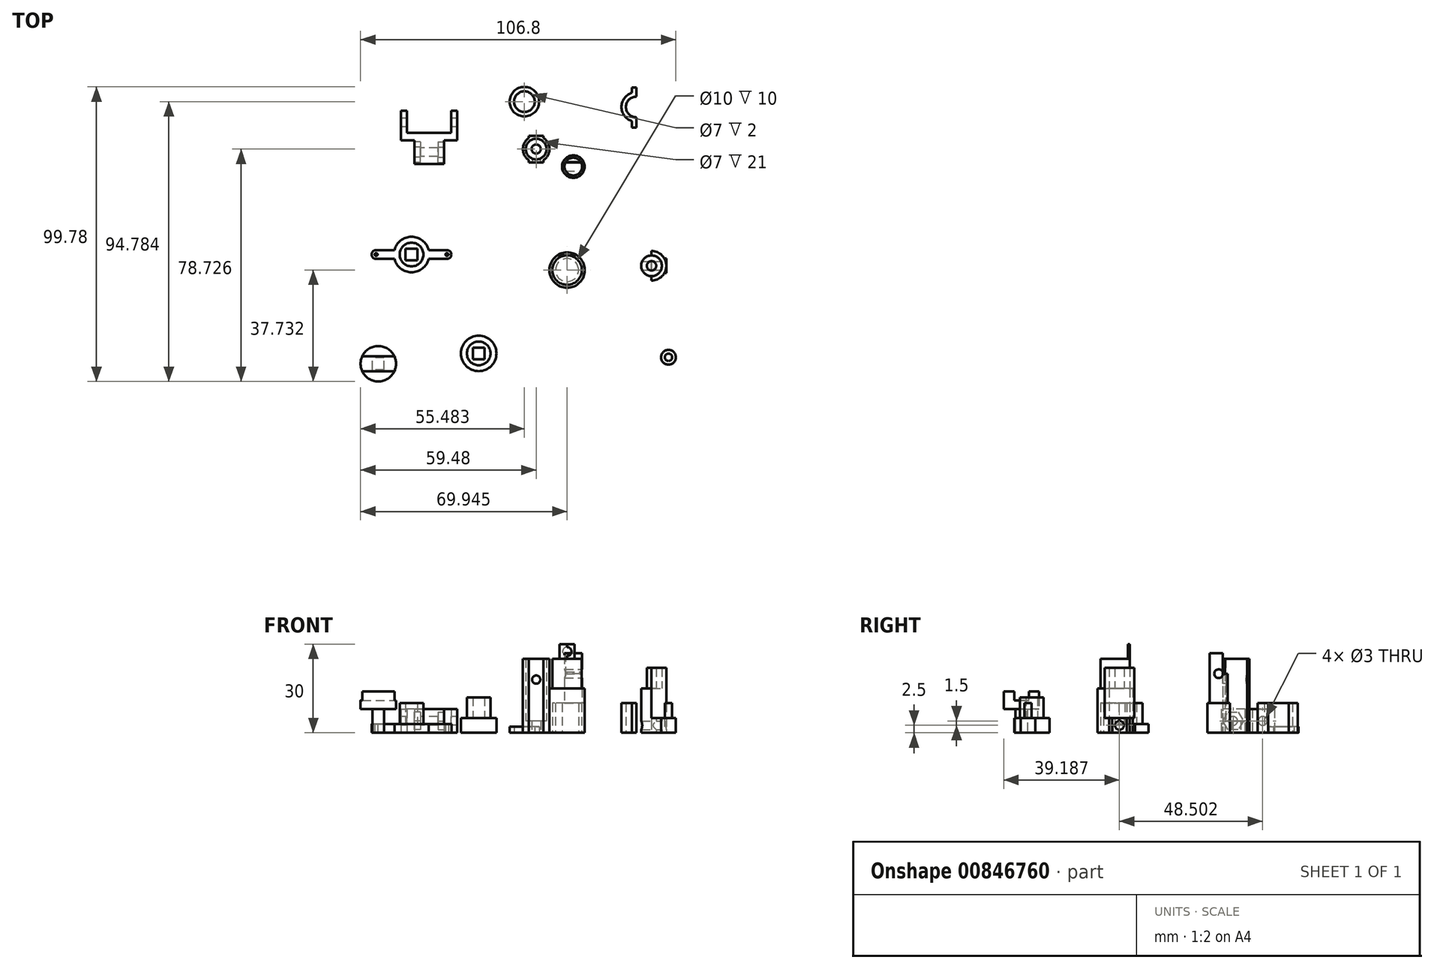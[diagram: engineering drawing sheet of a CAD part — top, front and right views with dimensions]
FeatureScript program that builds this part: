
annotation { "Feature Type Name" : "Feature", "Feature Type Description" : "" }
export const myFeature = defineFeature(function(context is Context, id is Id, definition is map)
    precondition{}
    {
        {
            var Q0;
            Q0=qCreatedBy(makeId("Top.planeOp"),FACE);
            var sketch = newSketch(context, id + "F0", { "sketchPlane" : qUnion([Q0])});
            skLineSegment(sketch, "E0.bottom", {"start": v(-39.48, 20.74) * mm, "end": v(-29.48, 20.74) * mm});
            skLineSegment(sketch, "E0.top", {"start": v(-39.48, 12.74) * mm, "end": v(-29.48, 12.74) * mm});
            skLineSegment(sketch, "E0.left", {"start": v(-39.48, 20.74) * mm, "end": v(-39.48, 12.74) * mm});
            skLineSegment(sketch, "E0.right", {"start": v(-29.48, 20.74) * mm, "end": v(-29.48, 12.74) * mm});
            skLineSegment(sketch, "E1", {"start": v(-39.48, 20.74) * mm, "end": v(-43.98, 20.74) * mm});
            skLineSegment(sketch, "E2", {"start": v(-29.48, 20.74) * mm, "end": v(-24.98, 20.74) * mm});
            skLineSegment(sketch, "E3", {"start": v(-43.98, 20.74) * mm, "end": v(-43.98, 30.74) * mm});
            skLineSegment(sketch, "E4", {"start": v(-24.98, 20.74) * mm, "end": v(-24.98, 30.74) * mm});
            skLineSegment(sketch, "E5", {"start": v(-24.98, 23.24) * mm, "end": v(-43.98, 23.24) * mm});
            skLineSegment(sketch, "E6", {"start": v(-26.98, 30.74) * mm, "end": v(-24.98, 30.74) * mm});
            skLineSegment(sketch, "E7", {"start": v(-43.98, 30.74) * mm, "end": v(-41.98, 30.74) * mm});
            skLineSegment(sketch, "E8", {"start": v(-41.98, 30.74) * mm, "end": v(-41.98, 23.24) * mm});
            skLineSegment(sketch, "E9", {"start": v(-26.98, 30.74) * mm, "end": v(-26.98, 23.24) * mm});
            skSolve(sketch);
        }
        {
            var Q0;
            Q0 = qSketchRegion(id + "F0", true);
            extrude(context, id + "F1", {"entities" : qUnion([Q0]), "depth" : 8 * mm, "offsetDistance" : 25 * mm});
        }
        {
            var Q0;
            Q0=makeQuery(id+"F1.opExtrude","SWEPT_FACE",FACE,{"disambiguationData":[OSD([sQuery(id+"F0.wireOp",EDGE,"E0.left")])]});
            var sketch = newSketch(context, id + "F2", { "sketchPlane" : qUnion([Q0])});
            skCircle(sketch, "E10", {"center": v(-16.74, 4) * mm, "radius": 1.5 * mm});
            skSolve(sketch);
        }
        {
            var Q0;
            Q0=makeQuery(id+"F2.imprint","IMPRINT",FACE,{"disambiguationData":[TD([[makeQuery(id+"F2.imprint","IMPRINT",EDGE,{"derivedFrom":sQuery(id+"F2.wireOp",EDGE,"E10")}),1.0]])]});
            extrude(context, id + "F3", {"entities" : qUnion([Q0]), "operationType" : NewBodyOperationType.REMOVE, "oppositeDirection" : true, "depth" : 25 * mm, "offsetDistance" : 25 * mm});
        }
        {
            var Q0;
            Q0=makeQuery(id+"F1.opExtrude","SWEPT_FACE",FACE,{"disambiguationData":[OSD([sQuery(id+"F0.wireOp",EDGE,"E3")])]});
            var sketch = newSketch(context, id + "F4", { "sketchPlane" : qUnion([Q0])});
            skCircle(sketch, "E11", {"center": v(-26.74, 4) * mm, "radius": 1.5 * mm});
            skSolve(sketch);
        }
        {
            var Q0;
            Q0=makeQuery(id+"F4.imprint","IMPRINT",FACE,{"disambiguationData":[TD([[makeQuery(id+"F4.imprint","IMPRINT",EDGE,{"derivedFrom":sQuery(id+"F4.wireOp",EDGE,"E11")}),1.0]])]});
            extrude(context, id + "F5", {"entities" : qUnion([Q0]), "operationType" : NewBodyOperationType.REMOVE, "oppositeDirection" : true, "depth" : 25 * mm, "offsetDistance" : 25 * mm});
        }
        {
            var Q0;
            Q0=qCreatedBy(makeId("Top.planeOp"),FACE);
            var sketch = newSketch(context, id + "F6", { "sketchPlane" : qUnion([Q0])});
            skCircle(sketch, "E12", {"center": v(40.86, -21.76) * mm, "radius": 5 * mm});
            skCircle(sketch, "E13", {"center": v(40.86, -21.76) * mm, "radius": 3.5 * mm});
            skCircle(sketch, "E14", {"center": v(40.86, -21.76) * mm, "radius": 1.6 * mm});
            skLineSegment(sketch, "E15", {"start": v(40.86, -26.76) * mm, "end": v(40.86, -16.76) * mm});
            skLineSegment(sketch, "E16", {"start": v(45.86, -21.76) * mm, "end": v(45.86, -19.26) * mm});
            skLineSegment(sketch, "E17", {"start": v(45.86, -21.76) * mm, "end": v(45.86, -24.26) * mm});
            skLineSegment(sketch, "E18", {"start": v(45.86, -19.26) * mm, "end": v(45.19, -19.26) * mm});
            skLineSegment(sketch, "E19", {"start": v(45.86, -24.26) * mm, "end": v(45.19, -24.26) * mm});
            skSolve(sketch);
        }
        {
            var Q0;
            Q0=makeQuery(id+"F6.imprint","IMPRINT",FACE,{"disambiguationData":[TD([[makeQuery(id+"F6.imprint","IMPRINT",EDGE,{"derivedFrom":sQuery(id+"F6.wireOp",EDGE,"E13")}),1.0]])]});
            extrude(context, id + "F7", {"entities" : qUnion([Q0]), "depth" : 15 * mm, "offsetDistance" : 25 * mm});
        }
        {
            var Q0;
            Q0=makeQuery(id+"F6.imprint","IMPRINT",FACE,{"disambiguationData":[TD([[makeQuery(id+"F6.imprint","IMPRINT",EDGE,{"derivedFrom":sQuery(id+"F6.wireOp",EDGE,"E12")}),1.0]])]});
            var Q1;
            Q1=makeQuery(id+"F6.imprint","IMPRINT",FACE,{"disambiguationData":[TD([[makeQuery(id+"F6.imprint","IMPRINT",EDGE,{"derivedFrom":sQuery(id+"F6.wireOp",EDGE,"E14")}),1.0]])]});
            var Q2;
            {var subQ0=sQuery(id+"F6.wireOp",EDGE,"E15");var subQ1=sQuery(id+"F6.wireOp",EDGE,"E12");var subQ2=makeQuery(id+"F6.imprint","INTERSECT",VERTEX,{"disambiguationData":[OD(0.0)],"derivedFrom":[subQ1,subQ0]});Q2=makeQuery(id+"F6.imprint","IMPRINT",FACE,{"disambiguationData":[TD([[makeQuery(id+"F6.imprint","IMPRINT",EDGE,{"disambiguationData":[TD([[subQ2,1.0]])],"derivedFrom":subQ1}),1.0]])]});}
            extrude(context, id + "F8", {"entities" : qUnion([Q0, Q1, Q2]), "operationType" : NewBodyOperationType.ADD, "depth" : 22 * mm, "offsetDistance" : 25 * mm});
        }
        {
            var Q0;
            {var subQ0=sQuery(id+"F6.wireOp",EDGE,"E15");var subQ1=sQuery(id+"F6.wireOp",EDGE,"E12");var subQ2=makeQuery(id+"F6.imprint","INTERSECT",VERTEX,{"disambiguationData":[OD(0.0)],"derivedFrom":[subQ1,subQ0]});Q0=makeQuery(id+"F6.imprint","IMPRINT",FACE,{"disambiguationData":[TD([[makeQuery(id+"F6.imprint","IMPRINT",EDGE,{"disambiguationData":[TD([[subQ2,1.0]])],"derivedFrom":subQ1}),1.0]])]});}
            var Q1;
            {var subQ0=sQuery(id+"F6.wireOp",EDGE,"E15");var subQ1=sQuery(id+"F6.wireOp",EDGE,"E14");var subQ2=makeQuery(id+"F6.imprint","INTERSECT",VERTEX,{"disambiguationData":[OD(0.0)],"derivedFrom":[subQ1,subQ0]});Q1=makeQuery(id+"F6.imprint","IMPRINT",FACE,{"disambiguationData":[TD([[makeQuery(id+"F6.imprint","IMPRINT",EDGE,{"disambiguationData":[TD([[subQ2,-1.0]])],"derivedFrom":subQ1}),1.0]])]});}
            extrude(context, id + "F9", {"entities" : qUnion([Q0, Q1]), "operationType" : NewBodyOperationType.REMOVE, "depth" : 5 * mm, "offsetDistance" : 25 * mm});
        }
        {
            var Q0;
            {var subQ0=sQuery(id+"F6.wireOp",EDGE,"E17");Q0=makeQuery(id+"F6.imprint","IMPRINT",FACE,{"disambiguationData":[TD([[makeQuery(id+"F6.imprint","IMPRINT",EDGE,{"derivedFrom":subQ0}),-1.0]])]});}
            var Q1;
            {var subQ0=sQuery(id+"F6.wireOp",EDGE,"E16");Q1=makeQuery(id+"F6.imprint","IMPRINT",FACE,{"disambiguationData":[TD([[makeQuery(id+"F6.imprint","IMPRINT",EDGE,{"derivedFrom":subQ0}),1.0]])]});}
            extrude(context, id + "F10", {"entities" : qUnion([Q0, Q1]), "operationType" : NewBodyOperationType.ADD, "depth" : 5 * mm, "offsetDistance" : 25 * mm});
        }
        {
            var Q0;
            Q0=makeQuery(id+"F10.boolean.opBoolean","MERGE",FACE,{"derivedFrom":[makeQuery(id+"F10.opExtrude","SWEPT_FACE",FACE,{"disambiguationData":[OSD([sQuery(id+"F6.wireOp",EDGE,"E16")])]}),makeQuery(id+"F10.opExtrude","SWEPT_FACE",FACE,{"disambiguationData":[OSD([sQuery(id+"F6.wireOp",EDGE,"E17")])]})]});
            var sketch = newSketch(context, id + "F11", { "sketchPlane" : qUnion([Q0])});
            skCircle(sketch, "E20", {"center": v(-21.76, 2.5) * mm, "radius": 1.5 * mm});
            skSolve(sketch);
        }
        {
            var Q0;
            Q0=makeQuery(id+"F11.imprint","IMPRINT",FACE,{"disambiguationData":[TD([[makeQuery(id+"F11.imprint","IMPRINT",EDGE,{"derivedFrom":sQuery(id+"F11.wireOp",EDGE,"E20")}),1.0]])]});
            extrude(context, id + "F12", {"entities" : qUnion([Q0]), "operationType" : NewBodyOperationType.REMOVE, "oppositeDirection" : true, "depth" : 25 * mm, "offsetDistance" : 25 * mm});
        }
        {
            var Q0;
            Q0=qCreatedBy(makeId("Top.planeOp"),FACE);
            var sketch = newSketch(context, id + "F13", { "sketchPlane" : qUnion([Q0])});
            skCircle(sketch, "E21", {"center": v(12.24, -23.22) * mm, "radius": 6 * mm});
            skCircle(sketch, "E22", {"center": v(12.24, -23.22) * mm, "radius": 5 * mm});
            skCircle(sketch, "E23", {"center": v(12.24, -23.22) * mm, "radius": 3.9 * mm});
            skSolve(sketch);
        }
        {
            var Q0;
            Q0=makeQuery(id+"F13.imprint","IMPRINT",FACE,{"disambiguationData":[TD([[makeQuery(id+"F13.imprint","IMPRINT",EDGE,{"derivedFrom":sQuery(id+"F13.wireOp",EDGE,"E23")}),1.0]])]});
            var Q1;
            Q1=makeQuery(id+"F13.imprint","IMPRINT",FACE,{"disambiguationData":[TD([[makeQuery(id+"F13.imprint","IMPRINT",EDGE,{"derivedFrom":sQuery(id+"F13.wireOp",EDGE,"E21")}),1.0]])]});
            var Q2;
            Q2=makeQuery(id+"F13.imprint","IMPRINT",FACE,{"disambiguationData":[TD([[makeQuery(id+"F13.imprint","IMPRINT",EDGE,{"derivedFrom":sQuery(id+"F13.wireOp",EDGE,"E22")}),1.0]])]});
            extrude(context, id + "F14", {"entities" : qUnion([Q0, Q1, Q2]), "depth" : 15 * mm, "offsetDistance" : 25 * mm});
        }
        {
            var Q0;
            Q0=makeQuery(id+"F13.imprint","IMPRINT",FACE,{"disambiguationData":[TD([[makeQuery(id+"F13.imprint","IMPRINT",EDGE,{"derivedFrom":sQuery(id+"F13.wireOp",EDGE,"E22")}),1.0]])]});
            extrude(context, id + "F15", {"entities" : qUnion([Q0]), "operationType" : NewBodyOperationType.REMOVE, "depth" : 10 * mm, "offsetDistance" : 25 * mm});
        }
        {
            var Q0;
            Q0=makeQuery(id+"F14.opExtrude","CAP_FACE",FACE,{"disambiguationData":[OSD([sQuery(id+"F13.wireOp",EDGE,"E21")])],"isStart":false});
            var sketch = newSketch(context, id + "F16", { "sketchPlane" : qUnion([Q0])});
            skCircle(sketch, "E24", {"center": v(12.24, -23.22) * mm, "radius": 5 * mm});
            skSolve(sketch);
        }
        {
            var Q0;
            Q0=makeQuery(id+"F16.imprint","IMPRINT",FACE,{"disambiguationData":[TD([[makeQuery(id+"F16.imprint","IMPRINT",EDGE,{"derivedFrom":sQuery(id+"F16.wireOp",EDGE,"E24")}),1.0]])]});
            extrude(context, id + "F17", {"entities" : qUnion([Q0]), "operationType" : NewBodyOperationType.ADD, "depth" : 10 * mm, "offsetDistance" : 25 * mm});
        }
        {
            var Q0;
            Q0=makeQuery(id+"F17.opExtrude","CAP_FACE",FACE,{"disambiguationData":[OSD([sQuery(id+"F16.wireOp",EDGE,"E24")])],"isStart":false});
            var sketch = newSketch(context, id + "F18", { "sketchPlane" : qUnion([Q0])});
            skLineSegment(sketch, "E25", {"start": v(12.24, -23.22) * mm, "end": v(7.24, -23.22) * mm});
            skLineSegment(sketch, "E26", {"start": v(7.24, -23.22) * mm, "end": v(17.24, -23.22) * mm});
            skCircle(sketch, "E27", {"center": v(12.24, -23.22) * mm, "radius": 3.5 * mm});
            skCircle(sketch, "E28", {"center": v(12.24, -23.22) * mm, "radius": 1.6 * mm});
            skLineSegment(sketch, "E29", {"start": v(12.24, -18.22) * mm, "end": v(9.74, -18.22) * mm});
            skLineSegment(sketch, "E30", {"start": v(12.24, -18.22) * mm, "end": v(14.74, -18.22) * mm});
            skLineSegment(sketch, "E31", {"start": v(14.74, -18.22) * mm, "end": v(14.74, -18.89) * mm});
            skLineSegment(sketch, "E32", {"start": v(9.74, -18.22) * mm, "end": v(9.74, -18.89) * mm});
            skSolve(sketch);
        }
        {
            var Q0;
            {var subQ0=sQuery(id+"F18.wireOp",EDGE,"E26");var subQ1=makeQuery(id+"F17.opExtrude","CAP_EDGE",EDGE,{"disambiguationData":[OSD([sQuery(id+"F16.wireOp",EDGE,"E24")])],"isStart":false});var subQ2=makeQuery(id+"F18.imprint","INTERSECT",VERTEX,{"disambiguationData":[OD(0.0)],"derivedFrom":[subQ1,subQ0]});Q0=makeQuery(id+"F18.imprint","IMPRINT",FACE,{"disambiguationData":[TD([[makeQuery(id+"F18.imprint","IMPRINT",EDGE,{"disambiguationData":[TD([[subQ2,-1.0]])],"derivedFrom":subQ0}),1.0]])]});}
            var Q1;
            {var subQ0=sQuery(id+"F18.wireOp",EDGE,"E26");var subQ1=makeQuery(id+"F18.imprint","IMPRINT",VERTEX,{"derivedFrom":subQ0});Q1=makeQuery(id+"F18.imprint","IMPRINT",FACE,{"disambiguationData":[TD([[makeQuery(id+"F18.imprint","IMPRINT",EDGE,{"disambiguationData":[TD([[subQ1,1.0]])],"derivedFrom":subQ0}),-1.0]])]});}
            var Q2;
            {var subQ0=sQuery(id+"F18.wireOp",EDGE,"E29");Q2=makeQuery(id+"F18.imprint","IMPRINT",FACE,{"disambiguationData":[TD([[makeQuery(id+"F18.imprint","IMPRINT",EDGE,{"derivedFrom":subQ0}),1.0]])]});}
            var Q3;
            {var subQ0=sQuery(id+"F18.wireOp",EDGE,"E30");Q3=makeQuery(id+"F18.imprint","IMPRINT",FACE,{"disambiguationData":[TD([[makeQuery(id+"F18.imprint","IMPRINT",EDGE,{"derivedFrom":subQ0}),-1.0]])]});}
            extrude(context, id + "F19", {"entities" : qUnion([Q0, Q1, Q2, Q3]), "operationType" : NewBodyOperationType.ADD, "depth" : 5 * mm, "offsetDistance" : 25 * mm});
        }
        {
            var Q0;
            Q0=makeQuery(id+"F19.opExtrude","SWEPT_FACE",FACE,{"disambiguationData":[OSD([sQuery(id+"F18.wireOp",EDGE,"E29"),sQuery(id+"F18.wireOp",EDGE,"E30")])]});
            var sketch = newSketch(context, id + "F20", { "sketchPlane" : qUnion([Q0])});
            skCircle(sketch, "E33", {"center": v(-12.24, 27.5) * mm, "radius": 1.5 * mm});
            skSolve(sketch);
        }
        {
            var Q0;
            Q0=makeQuery(id+"F20.imprint","IMPRINT",FACE,{"disambiguationData":[TD([[makeQuery(id+"F20.imprint","IMPRINT",EDGE,{"derivedFrom":sQuery(id+"F20.wireOp",EDGE,"E33")}),1.0]])]});
            extrude(context, id + "F21", {"entities" : qUnion([Q0]), "operationType" : NewBodyOperationType.REMOVE, "oppositeDirection" : true, "depth" : 25 * mm, "offsetDistance" : 25 * mm});
        }
        {
            var Q0;
            Q0=qCreatedBy(makeId("Top.planeOp"),FACE);
            var sketch = newSketch(context, id + "F22", { "sketchPlane" : qUnion([Q0])});
            skCircle(sketch, "E34", {"center": v(-52.45, -17.95) * mm, "radius": 1.5 * mm});
            skCircle(sketch, "E35", {"center": v(-28.45, -17.95) * mm, "radius": 1.5 * mm});
            skLineSegment(sketch, "E36", {"start": v(-52.45, -16.45) * mm, "end": v(-28.45, -16.45) * mm});
            skLineSegment(sketch, "E37", {"start": v(-28.45, -19.45) * mm, "end": v(-52.45, -19.45) * mm});
            skCircle(sketch, "E38", {"center": v(-52.45, -17.95) * mm, "radius": 0.5 * mm});
            skCircle(sketch, "E39", {"center": v(-28.45, -17.95) * mm, "radius": 0.5 * mm});
            skLineSegment(sketch, "E40", {"start": v(-52.45, -17.95) * mm, "end": v(-28.45, -17.95) * mm});
            skCircle(sketch, "E41", {"center": v(-40.45, -17.95) * mm, "radius": 6 * mm});
            skSolve(sketch);
        }
        {
            var Q0;
            Q0=makeQuery(id+"F22.imprint","IMPRINT",FACE,{"disambiguationData":[TD([[makeQuery(id+"F22.imprint","IMPRINT",EDGE,{"derivedFrom":sQuery(id+"F22.wireOp",EDGE,"E38")}),-1.0]])]});
            var Q1;
            {var subQ0=sQuery(id+"F22.wireOp",EDGE,"E36");Q1=makeQuery(id+"F22.imprint","IMPRINT",FACE,{"disambiguationData":[TD([[makeQuery(id+"F22.imprint","IMPRINT",EDGE,{"derivedFrom":subQ0}),-1.0]])]});}
            var Q2;
            Q2=makeQuery(id+"F22.imprint","IMPRINT",FACE,{"disambiguationData":[TD([[makeQuery(id+"F22.imprint","IMPRINT",EDGE,{"derivedFrom":sQuery(id+"F22.wireOp",EDGE,"E39")}),-1.0]])]});
            var Q3;
            {var subQ0=sQuery(id+"F22.wireOp",EDGE,"E37");var subQ1=sQuery(id+"F22.wireOp",EDGE,"E34");var subQ2=makeQuery(id+"F22.imprint","INTERSECT",VERTEX,{"derivedFrom":[subQ1,subQ0]});Q3=makeQuery(id+"F22.imprint","IMPRINT",FACE,{"disambiguationData":[TD([[makeQuery(id+"F22.imprint","IMPRINT",EDGE,{"disambiguationData":[TD([[subQ2,-1.0]])],"derivedFrom":subQ1}),-1.0]])]});}
            var Q4;
            {var subQ0=sQuery(id+"F22.wireOp",EDGE,"E41");var subQ1=sQuery(id+"F22.wireOp",EDGE,"E37");var subQ2=makeQuery(id+"F22.imprint","INTERSECT",VERTEX,{"disambiguationData":[OD(0.0)],"derivedFrom":[subQ1,subQ0]});Q4=makeQuery(id+"F22.imprint","IMPRINT",FACE,{"disambiguationData":[TD([[makeQuery(id+"F22.imprint","IMPRINT",EDGE,{"disambiguationData":[TD([[subQ2,-1.0]])],"derivedFrom":subQ1}),-1.0]])]});}
            var Q5;
            {var subQ0=sQuery(id+"F22.wireOp",EDGE,"E41");var subQ1=sQuery(id+"F22.wireOp",EDGE,"E37");var subQ2=makeQuery(id+"F22.imprint","INTERSECT",VERTEX,{"disambiguationData":[OD(0.0)],"derivedFrom":[subQ1,subQ0]});Q5=makeQuery(id+"F22.imprint","IMPRINT",FACE,{"disambiguationData":[TD([[makeQuery(id+"F22.imprint","IMPRINT",EDGE,{"disambiguationData":[TD([[subQ2,-1.0]])],"derivedFrom":subQ1}),1.0]])]});}
            var Q6;
            {var subQ0=sQuery(id+"F22.wireOp",EDGE,"E37");var subQ1=sQuery(id+"F22.wireOp",EDGE,"E35");var subQ2=makeQuery(id+"F22.imprint","INTERSECT",VERTEX,{"derivedFrom":[subQ1,subQ0]});Q6=makeQuery(id+"F22.imprint","IMPRINT",FACE,{"disambiguationData":[TD([[makeQuery(id+"F22.imprint","IMPRINT",EDGE,{"disambiguationData":[TD([[subQ2,1.0]])],"derivedFrom":subQ1}),-1.0]])]});}
            var Q7;
            {var subQ0=sQuery(id+"F22.wireOp",EDGE,"E41");var subQ1=sQuery(id+"F22.wireOp",EDGE,"E36");var subQ2=makeQuery(id+"F22.imprint","INTERSECT",VERTEX,{"disambiguationData":[OD(0.0)],"derivedFrom":[subQ1,subQ0]});Q7=makeQuery(id+"F22.imprint","IMPRINT",FACE,{"disambiguationData":[TD([[makeQuery(id+"F22.imprint","IMPRINT",EDGE,{"disambiguationData":[TD([[subQ2,-1.0]])],"derivedFrom":subQ1}),1.0]])]});}
            extrude(context, id + "F23", {"entities" : qUnion([Q0, Q1, Q2, Q3, Q4, Q5, Q6, Q7]), "depth" : 3 * mm, "offsetDistance" : 25 * mm});
        }
        {
            var Q0;
            Q0=makeQuery(id+"F23.opExtrude","CAP_FACE",FACE,{"disambiguationData":[OSD([sQuery(id+"F22.wireOp",EDGE,"E34"),sQuery(id+"F22.wireOp",EDGE,"E35"),sQuery(id+"F22.wireOp",EDGE,"E36"),sQuery(id+"F22.wireOp",EDGE,"E37"),sQuery(id+"F22.wireOp",EDGE,"E38"),sQuery(id+"F22.wireOp",EDGE,"E39"),sQuery(id+"F22.wireOp",EDGE,"E41")])],"isStart":false});
            var sketch = newSketch(context, id + "F24", { "sketchPlane" : qUnion([Q0])});
            skCircle(sketch, "E42", {"center": v(-40.45, -17.95) * mm, "radius": 4 * mm});
            skLineSegment(sketch, "E43.bottom", {"start": v(-38.45, -19.95) * mm, "end": v(-42.45, -19.95) * mm});
            skLineSegment(sketch, "E43.top", {"start": v(-38.45, -15.95) * mm, "end": v(-42.45, -15.95) * mm});
            skLineSegment(sketch, "E43.left", {"start": v(-38.45, -19.95) * mm, "end": v(-38.45, -15.95) * mm});
            skLineSegment(sketch, "E43.right", {"start": v(-42.45, -19.95) * mm, "end": v(-42.45, -15.95) * mm});
            skSolve(sketch);
        }
        {
            var Q0;
            Q0=makeQuery(id+"F24.imprint","IMPRINT",FACE,{"disambiguationData":[TD([[makeQuery(id+"F24.imprint","IMPRINT",EDGE,{"derivedFrom":sQuery(id+"F24.wireOp",EDGE,"E42")}),1.0]])]});
            extrude(context, id + "F25", {"entities" : qUnion([Q0]), "operationType" : NewBodyOperationType.ADD, "depth" : 7 * mm, "offsetDistance" : 25 * mm});
        }
        {
            var Q0;
            Q0=qCreatedBy(makeId("Top.planeOp"),FACE);
            var sketch = newSketch(context, id + "F26", { "sketchPlane" : qUnion([Q0])});
            skLineSegment(sketch, "E44.bottom", {"start": v(-49.7, -56.95) * mm, "end": v(-53.7, -56.95) * mm});
            skLineSegment(sketch, "E44.top", {"start": v(-49.7, -52.95) * mm, "end": v(-53.7, -52.95) * mm});
            skLineSegment(sketch, "E44.left", {"start": v(-49.7, -56.95) * mm, "end": v(-49.7, -52.95) * mm});
            skLineSegment(sketch, "E44.right", {"start": v(-53.7, -56.95) * mm, "end": v(-53.7, -52.95) * mm});
            skPoint(sketch, "E44.middle", {"position": v(-51.7, -54.95) * mm});
            skSolve(sketch);
        }
        {
            var Q0;
            Q0 = qSketchRegion(id + "F26", true);
            extrude(context, id + "F27", {"entities" : qUnion([Q0]), "depth" : 8 * mm, "offsetDistance" : 25 * mm});
        }
        {
            var Q0;
            Q0=makeQuery(id+"F27.opExtrude","CAP_FACE",FACE,{"disambiguationData":[OSD([sQuery(id+"F26.wireOp",EDGE,"E44.bottom"),sQuery(id+"F26.wireOp",EDGE,"E44.top"),sQuery(id+"F26.wireOp",EDGE,"E44.left"),sQuery(id+"F26.wireOp",EDGE,"E44.right")])],"isStart":false});
            var sketch = newSketch(context, id + "F28", { "sketchPlane" : qUnion([Q0])});
            skLineSegment(sketch, "E45", {"start": v(-51.7, -56.95) * mm, "end": v(-51.7, -52.95) * mm});
            skLineSegment(sketch, "E46", {"start": v(-53.7, -54.95) * mm, "end": v(-49.7, -54.95) * mm});
            skCircle(sketch, "E47", {"center": v(-51.7, -54.95) * mm, "radius": 6 * mm});
            skSolve(sketch);
        }
        {
            var Q0;
            {var subQ0=sQuery(id+"F28.wireOp",EDGE,"E45");var subQ1=makeQuery(id+"F27.opExtrude","CAP_EDGE",EDGE,{"disambiguationData":[OSD([sQuery(id+"F26.wireOp",EDGE,"E44.bottom")])],"isStart":false});var subQ2=makeQuery(id+"F28.imprint","INTERSECT",VERTEX,{"derivedFrom":[subQ1,subQ0]});Q0=makeQuery(id+"F28.imprint","IMPRINT",FACE,{"disambiguationData":[TD([[makeQuery(id+"F28.imprint","IMPRINT",EDGE,{"disambiguationData":[TD([[subQ2,-1.0]])],"derivedFrom":subQ0}),1.0]])]});}
            var Q1;
            {var subQ0=sQuery(id+"F28.wireOp",EDGE,"E45");var subQ1=makeQuery(id+"F27.opExtrude","CAP_EDGE",EDGE,{"disambiguationData":[OSD([sQuery(id+"F26.wireOp",EDGE,"E44.bottom")])],"isStart":false});var subQ2=makeQuery(id+"F28.imprint","INTERSECT",VERTEX,{"derivedFrom":[subQ1,subQ0]});Q1=makeQuery(id+"F28.imprint","IMPRINT",FACE,{"disambiguationData":[TD([[makeQuery(id+"F28.imprint","IMPRINT",EDGE,{"disambiguationData":[TD([[subQ2,-1.0]])],"derivedFrom":subQ0}),-1.0]])]});}
            var Q2;
            Q2=makeQuery(id+"F28.imprint","IMPRINT",FACE,{"disambiguationData":[TD([[makeQuery(id+"F28.imprint","IMPRINT",EDGE,{"derivedFrom":sQuery(id+"F28.wireOp",EDGE,"E47")}),1.0]])]});
            var Q3;
            {var subQ0=sQuery(id+"F28.wireOp",EDGE,"E45");var subQ1=makeQuery(id+"F27.opExtrude","CAP_EDGE",EDGE,{"disambiguationData":[OSD([sQuery(id+"F26.wireOp",EDGE,"E44.top")])],"isStart":false});var subQ2=makeQuery(id+"F28.imprint","INTERSECT",VERTEX,{"derivedFrom":[subQ1,subQ0]});Q3=makeQuery(id+"F28.imprint","IMPRINT",FACE,{"disambiguationData":[TD([[makeQuery(id+"F28.imprint","IMPRINT",EDGE,{"disambiguationData":[TD([[subQ2,1.0]])],"derivedFrom":subQ0}),-1.0]])]});}
            var Q4;
            {var subQ0=sQuery(id+"F28.wireOp",EDGE,"E45");var subQ1=makeQuery(id+"F27.opExtrude","CAP_EDGE",EDGE,{"disambiguationData":[OSD([sQuery(id+"F26.wireOp",EDGE,"E44.top")])],"isStart":false});var subQ2=makeQuery(id+"F28.imprint","INTERSECT",VERTEX,{"derivedFrom":[subQ1,subQ0]});Q4=makeQuery(id+"F28.imprint","IMPRINT",FACE,{"disambiguationData":[TD([[makeQuery(id+"F28.imprint","IMPRINT",EDGE,{"disambiguationData":[TD([[subQ2,1.0]])],"derivedFrom":subQ0}),1.0]])]});}
            extrude(context, id + "F29", {"entities" : qUnion([Q0, Q1, Q2, Q3, Q4]), "operationType" : NewBodyOperationType.ADD, "depth" : 6 * mm, "offsetDistance" : 25 * mm});
        }
        {
            var Q0;
            Q0=makeQuery(id+"F29.opExtrude","CAP_FACE",FACE,{"disambiguationData":[OSD([sQuery(id+"F28.wireOp",EDGE,"E47")])],"isStart":false});
            var sketch = newSketch(context, id + "F30", { "sketchPlane" : qUnion([Q0])});
            skLineSegment(sketch, "E48", {"start": v(-57.16, -57.45) * mm, "end": v(-46.26, -57.45) * mm});
            skLineSegment(sketch, "E49", {"start": v(-57.16, -52.45) * mm, "end": v(-46.26, -52.45) * mm});
            skSolve(sketch);
        }
        {
            var Q0;
            {var subQ0=sQuery(id+"F30.wireOp",EDGE,"E48");Q0=makeQuery(id+"F30.imprint","IMPRINT",FACE,{"disambiguationData":[TD([[makeQuery(id+"F30.imprint","IMPRINT",EDGE,{"derivedFrom":subQ0}),1.0]])]});}
            extrude(context, id + "F31", {"entities" : qUnion([Q0]), "operationType" : NewBodyOperationType.REMOVE, "oppositeDirection" : true, "depth" : 3 * mm, "offsetDistance" : 25 * mm});
        }
        {
            var Q0;
            Q0=qCreatedBy(makeId("Top.planeOp"),FACE);
            var sketch = newSketch(context, id + "F32", { "sketchPlane" : qUnion([Q0])});
            skCircle(sketch, "E50", {"center": v(-17.7, -51.45) * mm, "radius": 6 * mm});
            skSolve(sketch);
        }
        {
            var Q0;
            Q0=makeQuery(id+"F32.imprint","IMPRINT",FACE,{"disambiguationData":[TD([[makeQuery(id+"F32.imprint","IMPRINT",EDGE,{"derivedFrom":sQuery(id+"F32.wireOp",EDGE,"E50")}),1.0]])]});
            extrude(context, id + "F33", {"entities" : qUnion([Q0]), "depth" : 5 * mm, "offsetDistance" : 25 * mm});
        }
        {
            var Q0;
            Q0=makeQuery(id+"F33.opExtrude","CAP_FACE",FACE,{"disambiguationData":[OSD([sQuery(id+"F32.wireOp",EDGE,"E50")])],"isStart":false});
            var sketch = newSketch(context, id + "F34", { "sketchPlane" : qUnion([Q0])});
            skLineSegment(sketch, "E51.bottom", {"start": v(-15.7, -53.45) * mm, "end": v(-19.7, -53.45) * mm});
            skLineSegment(sketch, "E51.top", {"start": v(-15.7, -49.45) * mm, "end": v(-19.7, -49.45) * mm});
            skLineSegment(sketch, "E51.left", {"start": v(-15.7, -53.45) * mm, "end": v(-15.7, -49.45) * mm});
            skLineSegment(sketch, "E51.right", {"start": v(-19.7, -53.45) * mm, "end": v(-19.7, -49.45) * mm});
            skPoint(sketch, "E51.middle", {"position": v(-17.7, -51.45) * mm});
            skCircle(sketch, "E52", {"center": v(-17.7, -51.45) * mm, "radius": 4 * mm});
            skSolve(sketch);
        }
        {
            var Q0;
            Q0=makeQuery(id+"F34.imprint","IMPRINT",FACE,{"disambiguationData":[TD([[makeQuery(id+"F34.imprint","IMPRINT",EDGE,{"derivedFrom":sQuery(id+"F34.wireOp",EDGE,"E51.bottom")}),1.0]])]});
            extrude(context, id + "F35", {"entities" : qUnion([Q0]), "operationType" : NewBodyOperationType.ADD, "depth" : 7 * mm, "offsetDistance" : 25 * mm});
        }
        {
            var Q0;
            Q0=qCreatedBy(makeId("Top.planeOp"),FACE);
            var sketch = newSketch(context, id + "F36", { "sketchPlane" : qUnion([Q0])});
            skCircle(sketch, "E53", {"center": v(35.66, 32.04) * mm, "radius": 5 * mm});
            skCircle(sketch, "E54", {"center": v(35.66, 32.04) * mm, "radius": 3.5 * mm});
            skLineSegment(sketch, "E55", {"start": v(35.66, 32.04) * mm, "end": v(35.66, 25.08) * mm});
            skLineSegment(sketch, "E56", {"start": v(35.66, 25.08) * mm, "end": v(34.16, 25.08) * mm});
            skLineSegment(sketch, "E57", {"start": v(34.16, 25.08) * mm, "end": v(34.16, 38.67) * mm});
            skLineSegment(sketch, "E58", {"start": v(34.16, 38.67) * mm, "end": v(35.66, 38.67) * mm});
            skLineSegment(sketch, "E59", {"start": v(35.66, 38.67) * mm, "end": v(35.66, 32.04) * mm});
            skSolve(sketch);
        }
        {
            var Q0;
            {var subQ5=sQuery(id+"F36.wireOp",EDGE,"E56");Q0=makeQuery(id+"F36.imprint","IMPRINT",FACE,{"disambiguationData":[TD([[makeQuery(id+"F36.imprint","IMPRINT",EDGE,{"derivedFrom":subQ5}),-1.0]])]});}
            var Q1;
            {var subQ0=sQuery(id+"F36.wireOp",EDGE,"E57");var subQ1=sQuery(id+"F36.wireOp",EDGE,"E53");var subQ2=makeQuery(id+"F36.imprint","INTERSECT",VERTEX,{"disambiguationData":[OD(1.0)],"derivedFrom":[subQ1,subQ0]});Q1=makeQuery(id+"F36.imprint","IMPRINT",FACE,{"disambiguationData":[TD([[makeQuery(id+"F36.imprint","IMPRINT",EDGE,{"disambiguationData":[TD([[subQ2,-1.0]])],"derivedFrom":subQ1}),1.0]])]});}
            var Q2;
            {var subQ0=sQuery(id+"F36.wireOp",EDGE,"E57");var subQ1=sQuery(id+"F36.wireOp",EDGE,"E53");var subQ2=makeQuery(id+"F36.imprint","INTERSECT",VERTEX,{"disambiguationData":[OD(0.0)],"derivedFrom":[subQ1,subQ0]});Q2=makeQuery(id+"F36.imprint","IMPRINT",FACE,{"disambiguationData":[TD([[makeQuery(id+"F36.imprint","IMPRINT",EDGE,{"disambiguationData":[TD([[subQ2,-1.0]])],"derivedFrom":subQ1}),1.0]])]});}
            var Q3;
            {var subQ0=sQuery(id+"F36.wireOp",EDGE,"E57");var subQ1=sQuery(id+"F36.wireOp",EDGE,"E53");var subQ2=makeQuery(id+"F36.imprint","INTERSECT",VERTEX,{"disambiguationData":[OD(0.0)],"derivedFrom":[subQ1,subQ0]});Q3=makeQuery(id+"F36.imprint","IMPRINT",FACE,{"disambiguationData":[TD([[makeQuery(id+"F36.imprint","IMPRINT",EDGE,{"disambiguationData":[TD([[subQ2,1.0]])],"derivedFrom":subQ1}),1.0]])]});}
            var Q4;
            {var subQ5=sQuery(id+"F36.wireOp",EDGE,"E58");Q4=makeQuery(id+"F36.imprint","IMPRINT",FACE,{"disambiguationData":[TD([[makeQuery(id+"F36.imprint","IMPRINT",EDGE,{"derivedFrom":subQ5}),-1.0]])]});}
            extrude(context, id + "F37", {"entities" : qUnion([Q0, Q1, Q2, Q3, Q4]), "depth" : 10 * mm, "offsetDistance" : 25 * mm});
        }
        {
            var Q0;
            Q0=qCreatedBy(makeId("Top.planeOp"),FACE);
            var sketch = newSketch(context, id + "F38", { "sketchPlane" : qUnion([Q0])});
            skCircle(sketch, "E60", {"center": v(1.77, 17.78) * mm, "radius": 4.5 * mm});
            skCircle(sketch, "E61", {"center": v(1.77, 17.78) * mm, "radius": 3.5 * mm});
            skCircle(sketch, "E62", {"center": v(1.77, 17.78) * mm, "radius": 1.55 * mm});
            skLineSegment(sketch, "E63.bottom", {"start": v(4.27, 22.28) * mm, "end": v(-0.73, 22.28) * mm});
            skLineSegment(sketch, "E63.top", {"start": v(4.27, 13.28) * mm, "end": v(-0.73, 13.28) * mm});
            skLineSegment(sketch, "E63.left", {"start": v(4.27, 22.28) * mm, "end": v(4.27, 13.28) * mm});
            skLineSegment(sketch, "E63.right", {"start": v(-0.73, 22.28) * mm, "end": v(-0.73, 13.28) * mm});
            skSolve(sketch);
        }
        {
            var Q0;
            Q0=makeQuery(id+"F38.imprint","IMPRINT",FACE,{"disambiguationData":[TD([[makeQuery(id+"F38.imprint","IMPRINT",EDGE,{"derivedFrom":sQuery(id+"F38.wireOp",EDGE,"E60")}),1.0]])]});
            var Q1;
            {var subQ0=sQuery(id+"F38.wireOp",EDGE,"E63.left");var subQ1=sQuery(id+"F38.wireOp",EDGE,"E60");var subQ2=makeQuery(id+"F38.imprint","INTERSECT",VERTEX,{"disambiguationData":[OD(0.0)],"derivedFrom":[subQ1,subQ0]});Q1=makeQuery(id+"F38.imprint","IMPRINT",FACE,{"disambiguationData":[TD([[makeQuery(id+"F38.imprint","IMPRINT",EDGE,{"disambiguationData":[TD([[subQ2,1.0]])],"derivedFrom":subQ1}),1.0]])]});}
            var Q2;
            {var subQ0=sQuery(id+"F38.wireOp",EDGE,"E63.right");var subQ1=sQuery(id+"F38.wireOp",EDGE,"E60");var subQ2=makeQuery(id+"F38.imprint","INTERSECT",VERTEX,{"disambiguationData":[OD(0.0)],"derivedFrom":[subQ1,subQ0]});Q2=makeQuery(id+"F38.imprint","IMPRINT",FACE,{"disambiguationData":[TD([[makeQuery(id+"F38.imprint","IMPRINT",EDGE,{"disambiguationData":[TD([[subQ2,-1.0]])],"derivedFrom":subQ1}),1.0]])]});}
            var Q3;
            {var subQ0=sQuery(id+"F38.wireOp",EDGE,"E63.top");var subQ1=sQuery(id+"F38.wireOp",EDGE,"E60");var subQ2=makeQuery(id+"F38.imprint","INTERSECT",VERTEX,{"derivedFrom":[subQ1,subQ0]});Q3=makeQuery(id+"F38.imprint","IMPRINT",FACE,{"disambiguationData":[TD([[makeQuery(id+"F38.imprint","IMPRINT",EDGE,{"disambiguationData":[TD([[subQ2,-1.0]])],"derivedFrom":subQ1}),-1.0]])]});}
            var Q4;
            {var subQ0=sQuery(id+"F38.wireOp",EDGE,"E63.bottom");var subQ1=sQuery(id+"F38.wireOp",EDGE,"E60");var subQ2=makeQuery(id+"F38.imprint","INTERSECT",VERTEX,{"derivedFrom":[subQ1,subQ0]});Q4=makeQuery(id+"F38.imprint","IMPRINT",FACE,{"disambiguationData":[TD([[makeQuery(id+"F38.imprint","IMPRINT",EDGE,{"disambiguationData":[TD([[subQ2,1.0]])],"derivedFrom":subQ1}),-1.0]])]});}
            var Q5;
            {var subQ0=sQuery(id+"F38.wireOp",EDGE,"E63.bottom");var subQ1=sQuery(id+"F38.wireOp",EDGE,"E60");var subQ2=makeQuery(id+"F38.imprint","INTERSECT",VERTEX,{"derivedFrom":[subQ1,subQ0]});Q5=makeQuery(id+"F38.imprint","IMPRINT",FACE,{"disambiguationData":[TD([[makeQuery(id+"F38.imprint","IMPRINT",EDGE,{"disambiguationData":[TD([[subQ2,-1.0]])],"derivedFrom":subQ1}),-1.0]])]});}
            var Q6;
            {var subQ0=sQuery(id+"F38.wireOp",EDGE,"E63.right");var subQ1=sQuery(id+"F38.wireOp",EDGE,"E60");var subQ2=makeQuery(id+"F38.imprint","INTERSECT",VERTEX,{"disambiguationData":[OD(1.0)],"derivedFrom":[subQ1,subQ0]});Q6=makeQuery(id+"F38.imprint","IMPRINT",FACE,{"disambiguationData":[TD([[makeQuery(id+"F38.imprint","IMPRINT",EDGE,{"disambiguationData":[TD([[subQ2,-1.0]])],"derivedFrom":subQ1}),-1.0]])]});}
            extrude(context, id + "F39", {"entities" : qUnion([Q0, Q1, Q2, Q3, Q4, Q5, Q6]), "depth" : 25 * mm, "offsetDistance" : 25 * mm});
        }
        {
            var Q0;
            Q0=makeQuery(id+"F38.imprint","IMPRINT",FACE,{"disambiguationData":[TD([[makeQuery(id+"F38.imprint","IMPRINT",EDGE,{"derivedFrom":sQuery(id+"F38.wireOp",EDGE,"E61")}),1.0]])]});
            var Q1;
            {var subQ0=sQuery(id+"F38.wireOp",EDGE,"E63.left");var subQ1=sQuery(id+"F38.wireOp",EDGE,"E61");var subQ2=makeQuery(id+"F38.imprint","INTERSECT",VERTEX,{"disambiguationData":[OD(0.0)],"derivedFrom":[subQ1,subQ0]});Q1=makeQuery(id+"F38.imprint","IMPRINT",FACE,{"disambiguationData":[TD([[makeQuery(id+"F38.imprint","IMPRINT",EDGE,{"disambiguationData":[TD([[subQ2,1.0]])],"derivedFrom":subQ1}),1.0]])]});}
            var Q2;
            {var subQ0=sQuery(id+"F38.wireOp",EDGE,"E63.right");var subQ1=sQuery(id+"F38.wireOp",EDGE,"E61");var subQ2=makeQuery(id+"F38.imprint","INTERSECT",VERTEX,{"disambiguationData":[OD(0.0)],"derivedFrom":[subQ1,subQ0]});Q2=makeQuery(id+"F38.imprint","IMPRINT",FACE,{"disambiguationData":[TD([[makeQuery(id+"F38.imprint","IMPRINT",EDGE,{"disambiguationData":[TD([[subQ2,-1.0]])],"derivedFrom":subQ1}),1.0]])]});}
            extrude(context, id + "F40", {"entities" : qUnion([Q0, Q1, Q2]), "operationType" : NewBodyOperationType.ADD, "depth" : 4 * mm, "offsetDistance" : 25 * mm});
        }
        {
            var Q0;
            Q0=makeQuery(id+"F39.opExtrude","SWEPT_FACE",FACE,{"disambiguationData":[OSD([sQuery(id+"F38.wireOp",EDGE,"E63.top")])]});
            var sketch = newSketch(context, id + "F41", { "sketchPlane" : qUnion([Q0])});
            skCircle(sketch, "E64", {"center": v(1.77, 18) * mm, "radius": 1.4 * mm});
            skPoint(sketch, "E64.centerSnap0", {"position": v(1.77, 0) * mm});
            skSolve(sketch);
        }
        {
            var Q0;
            Q0=makeQuery(id+"F41.imprint","IMPRINT",FACE,{"disambiguationData":[TD([[makeQuery(id+"F41.imprint","IMPRINT",EDGE,{"derivedFrom":sQuery(id+"F41.wireOp",EDGE,"E64")}),1.0]])]});
            extrude(context, id + "F42", {"entities" : qUnion([Q0]), "operationType" : NewBodyOperationType.REMOVE, "oppositeDirection" : true, "depth" : 8 * mm, "offsetDistance" : 25 * mm});
        }
        {
            var Q0;
            Q0=qCreatedBy(makeId("Top.planeOp"),FACE);
            var sketch = newSketch(context, id + "F43", { "sketchPlane" : qUnion([Q0])});
            skCircle(sketch, "E65", {"center": v(14.36, 11.83) * mm, "radius": 3.8 * mm});
            skSolve(sketch);
        }
        {
            var Q0;
            Q0 = qSketchRegion(id + "F43", true);
            extrude(context, id + "F44", {"entities" : qUnion([Q0]), "depth" : 10 * mm, "offsetDistance" : 25 * mm});
        }
        {
            var Q0;
            Q0=qCreatedBy(makeId("Top.planeOp"),FACE);
            var sketch = newSketch(context, id + "F45", { "sketchPlane" : qUnion([Q0])});
            skCircle(sketch, "E66", {"center": v(-2.23, 33.83) * mm, "radius": 5 * mm});
            skCircle(sketch, "E67", {"center": v(-2.23, 33.83) * mm, "radius": 3.5 * mm});
            skSolve(sketch);
        }
        {
            var Q0;
            Q0=makeQuery(id+"F45.imprint","IMPRINT",FACE,{"disambiguationData":[TD([[makeQuery(id+"F45.imprint","IMPRINT",EDGE,{"derivedFrom":sQuery(id+"F45.wireOp",EDGE,"E66")}),1.0]])]});
            extrude(context, id + "F46", {"entities" : qUnion([Q0]), "depth" : 2 * mm, "offsetDistance" : 25 * mm});
        }
        {
            var Q0;
            Q0=makeQuery(id+"F44.opExtrude","CAP_FACE",FACE,{"disambiguationData":[OSD([sQuery(id+"F43.wireOp",EDGE,"E65")])],"isStart":false});
            var sketch = newSketch(context, id + "F47", { "sketchPlane" : qUnion([Q0])});
            skCircle(sketch, "E68", {"center": v(14.36, 11.83) * mm, "radius": 3 * mm});
            skSolve(sketch);
        }
        {
            var Q0;
            Q0=makeQuery(id+"F47.imprint","IMPRINT",FACE,{"disambiguationData":[TD([[makeQuery(id+"F47.imprint","IMPRINT",EDGE,{"derivedFrom":sQuery(id+"F47.wireOp",EDGE,"E68")}),1.0]])]});
            extrude(context, id + "F48", {"entities" : qUnion([Q0]), "operationType" : NewBodyOperationType.ADD, "depth" : 10 * mm, "offsetDistance" : 25 * mm});
        }
        {
            var Q0;
            Q0=makeQuery(id+"F48.opExtrude","CAP_FACE",FACE,{"disambiguationData":[OSD([sQuery(id+"F47.wireOp",EDGE,"E68")])],"isStart":false});
            var sketch = newSketch(context, id + "F49", { "sketchPlane" : qUnion([Q0])});
            skCircle(sketch, "E69", {"center": v(14.36, 11.83) * mm, "radius": 3 * mm});
            skLineSegment(sketch, "E70.bottom", {"start": v(11.36, 13.23) * mm, "end": v(17.36, 13.23) * mm});
            skLineSegment(sketch, "E70.top", {"start": v(11.36, 10.43) * mm, "end": v(17.36, 10.43) * mm});
            skLineSegment(sketch, "E70.left", {"start": v(11.36, 13.23) * mm, "end": v(11.36, 10.43) * mm});
            skLineSegment(sketch, "E70.right", {"start": v(17.36, 13.23) * mm, "end": v(17.36, 10.43) * mm});
            skLineSegment(sketch, "E71", {"start": v(14.36, 11.83) * mm, "end": v(11.36, 11.83) * mm});
            skSolve(sketch);
        }
        {
            var Q0;
            Q0=makeQuery(id+"F49.imprint","IMPRINT",FACE,{"disambiguationData":[TD([[makeQuery(id+"F49.imprint","IMPRINT",EDGE,{"derivedFrom":sQuery(id+"F49.wireOp",EDGE,"E69")}),1.0]])]});
            var Q1;
            {var subQ0=sQuery(id+"F49.wireOp",EDGE,"E70.bottom");var subQ1=sQuery(id+"F49.wireOp",EDGE,"E69");var subQ2=makeQuery(id+"F49.imprint","INTERSECT",VERTEX,{"disambiguationData":[OD(0.0)],"derivedFrom":[subQ1,subQ0]});Q1=makeQuery(id+"F49.imprint","IMPRINT",FACE,{"disambiguationData":[TD([[makeQuery(id+"F49.imprint","IMPRINT",EDGE,{"disambiguationData":[TD([[subQ2,-1.0]])],"derivedFrom":subQ1}),1.0]])]});}
            var Q2;
            {var subQ0=sQuery(id+"F49.wireOp",EDGE,"E70.top");var subQ1=sQuery(id+"F49.wireOp",EDGE,"E69");var subQ2=makeQuery(id+"F49.imprint","INTERSECT",VERTEX,{"disambiguationData":[OD(0.0)],"derivedFrom":[subQ1,subQ0]});Q2=makeQuery(id+"F49.imprint","IMPRINT",FACE,{"disambiguationData":[TD([[makeQuery(id+"F49.imprint","IMPRINT",EDGE,{"disambiguationData":[TD([[subQ2,-1.0]])],"derivedFrom":subQ1}),1.0]])]});}
            extrude(context, id + "F50", {"entities" : qUnion([Q0, Q1, Q2]), "operationType" : NewBodyOperationType.ADD, "depth" : 7 * mm, "offsetDistance" : 25 * mm});
        }
        {
            var Q0;
            Q0=sQuery(id+"F49.wireOp",EDGE,"E70.right");
            cPlane(context, id + "F51", {"entities" : qUnion([Q0]), "cplaneType" : CPlaneType.LINE_ANGLE, "offset" : 25 * mm, "angle" : 90 * degree, "oppositeDirection" : true, "width" : 150 * mm, "height" : 150 * mm});
        }
        {
            var Q0;
            Q0=qCreatedBy(id+"F51.planeOp",FACE);
            var sketch = newSketch(context, id + "F52", { "sketchPlane" : qUnion([Q0])});
            skCircle(sketch, "E72", {"center": v(-11.83, 20) * mm, "radius": 1.5 * mm});
            skSolve(sketch);
        }
        {
            var Q0;
            Q0=makeQuery(id+"F52.imprint","IMPRINT",FACE,{"disambiguationData":[TD([[makeQuery(id+"F52.imprint","IMPRINT",EDGE,{"derivedFrom":sQuery(id+"F52.wireOp",EDGE,"E72")}),1.0]])]});
            extrude(context, id + "F53", {"entities" : qUnion([Q0]), "operationType" : NewBodyOperationType.REMOVE, "depth" : 6 * mm, "offsetDistance" : 25 * mm});
        }
        {
            var Q0;
            Q0=qCreatedBy(makeId("Top.planeOp"),FACE);
            var sketch = newSketch(context, id + "F54", { "sketchPlane" : qUnion([Q0])});
            skCircle(sketch, "E73", {"center": v(46.6, -52.76) * mm, "radius": 2.5 * mm});
            skCircle(sketch, "E74", {"center": v(46.6, -52.76) * mm, "radius": 1.25 * mm});
            skSolve(sketch);
        }
        {
            var Q0;
            Q0=makeQuery(id+"F54.imprint","IMPRINT",FACE,{"disambiguationData":[TD([[makeQuery(id+"F54.imprint","IMPRINT",EDGE,{"derivedFrom":sQuery(id+"F54.wireOp",EDGE,"E73")}),1.0]])]});
            extrude(context, id + "F55", {"entities" : qUnion([Q0]), "depth" : 5 * mm, "offsetDistance" : 25 * mm});
        }
        {
            var Q0;
            Q0=makeQuery(id+"F54.imprint","IMPRINT",FACE,{"disambiguationData":[TD([[makeQuery(id+"F54.imprint","IMPRINT",EDGE,{"derivedFrom":sQuery(id+"F54.wireOp",EDGE,"E74")}),1.0]])]});
            extrude(context, id + "F56", {"entities" : qUnion([Q0]), "operationType" : NewBodyOperationType.ADD, "depth" : 10 * mm, "offsetDistance" : 25 * mm});
        }
        {
            var Q0;
            Q0=makeQuery(id+"F1.opExtrude","SWEPT_FACE",FACE,{"disambiguationData":[OSD([sQuery(id+"F0.wireOp",EDGE,"E0.left")])]});
            var sketch = newSketch(context, id + "F57", { "sketchPlane" : qUnion([Q0])});
            skCircle(sketch, "E75.cCircle", {"center": v(-16.74, 4) * mm, "radius": 3 * mm, "construction": true});
            skLineSegment(sketch, "E75.0", {"start": v(-15, 1) * mm, "end": v(-18.47, 1) * mm});
            skLineSegment(sketch, "E75.1", {"start": v(-18.47, 1) * mm, "end": v(-20.2, 4) * mm});
            skLineSegment(sketch, "E75.2", {"start": v(-20.2, 4) * mm, "end": v(-18.47, 7) * mm});
            skLineSegment(sketch, "E75.3", {"start": v(-18.47, 7) * mm, "end": v(-15, 7) * mm});
            skLineSegment(sketch, "E75.4", {"start": v(-15, 7) * mm, "end": v(-13.27, 4) * mm});
            skLineSegment(sketch, "E75.5", {"start": v(-13.27, 4) * mm, "end": v(-15, 1) * mm});
            skPoint(sketch, "E75.0.midPoint", {"position": v(-16.74, 1) * mm});
            skSolve(sketch);
        }
        {
            var Q0;
            Q0=makeQuery(id+"F57.imprint","IMPRINT",FACE,{"disambiguationData":[TD([[makeQuery(id+"F57.imprint","IMPRINT",EDGE,{"derivedFrom":sQuery(id+"F57.wireOp",EDGE,"E75.0")}),-1.0]])]});
            extrude(context, id + "F58", {"entities" : qUnion([Q0]), "operationType" : NewBodyOperationType.REMOVE, "oppositeDirection" : true, "depth" : 2 * mm, "offsetDistance" : 25 * mm});
        }
        {
            var Q0;
            Q0=makeQuery(id+"F1.opExtrude","SWEPT_FACE",FACE,{"disambiguationData":[OSD([sQuery(id+"F0.wireOp",EDGE,"E0.right")])]});
            var sketch = newSketch(context, id + "F59", { "sketchPlane" : qUnion([Q0])});
            skCircle(sketch, "E76.cCircle", {"center": v(16.74, 4) * mm, "radius": 3 * mm, "construction": true});
            skLineSegment(sketch, "E76.0", {"start": v(18.47, 1) * mm, "end": v(15, 1) * mm});
            skLineSegment(sketch, "E76.1", {"start": v(15, 1) * mm, "end": v(13.27, 4) * mm});
            skLineSegment(sketch, "E76.2", {"start": v(13.27, 4) * mm, "end": v(15, 7) * mm});
            skLineSegment(sketch, "E76.3", {"start": v(15, 7) * mm, "end": v(18.47, 7) * mm});
            skLineSegment(sketch, "E76.4", {"start": v(18.47, 7) * mm, "end": v(20.2, 4) * mm});
            skLineSegment(sketch, "E76.5", {"start": v(20.2, 4) * mm, "end": v(18.47, 1) * mm});
            skPoint(sketch, "E76.0.midPoint", {"position": v(16.74, 1) * mm});
            skSolve(sketch);
        }
        {
            var Q0;
            Q0=makeQuery(id+"F59.imprint","IMPRINT",FACE,{"disambiguationData":[TD([[makeQuery(id+"F59.imprint","IMPRINT",EDGE,{"derivedFrom":sQuery(id+"F59.wireOp",EDGE,"E76.0")}),-1.0]])]});
            extrude(context, id + "F60", {"entities" : qUnion([Q0]), "operationType" : NewBodyOperationType.REMOVE, "oppositeDirection" : true, "depth" : 2 * mm, "offsetDistance" : 25 * mm});
        }
    });
